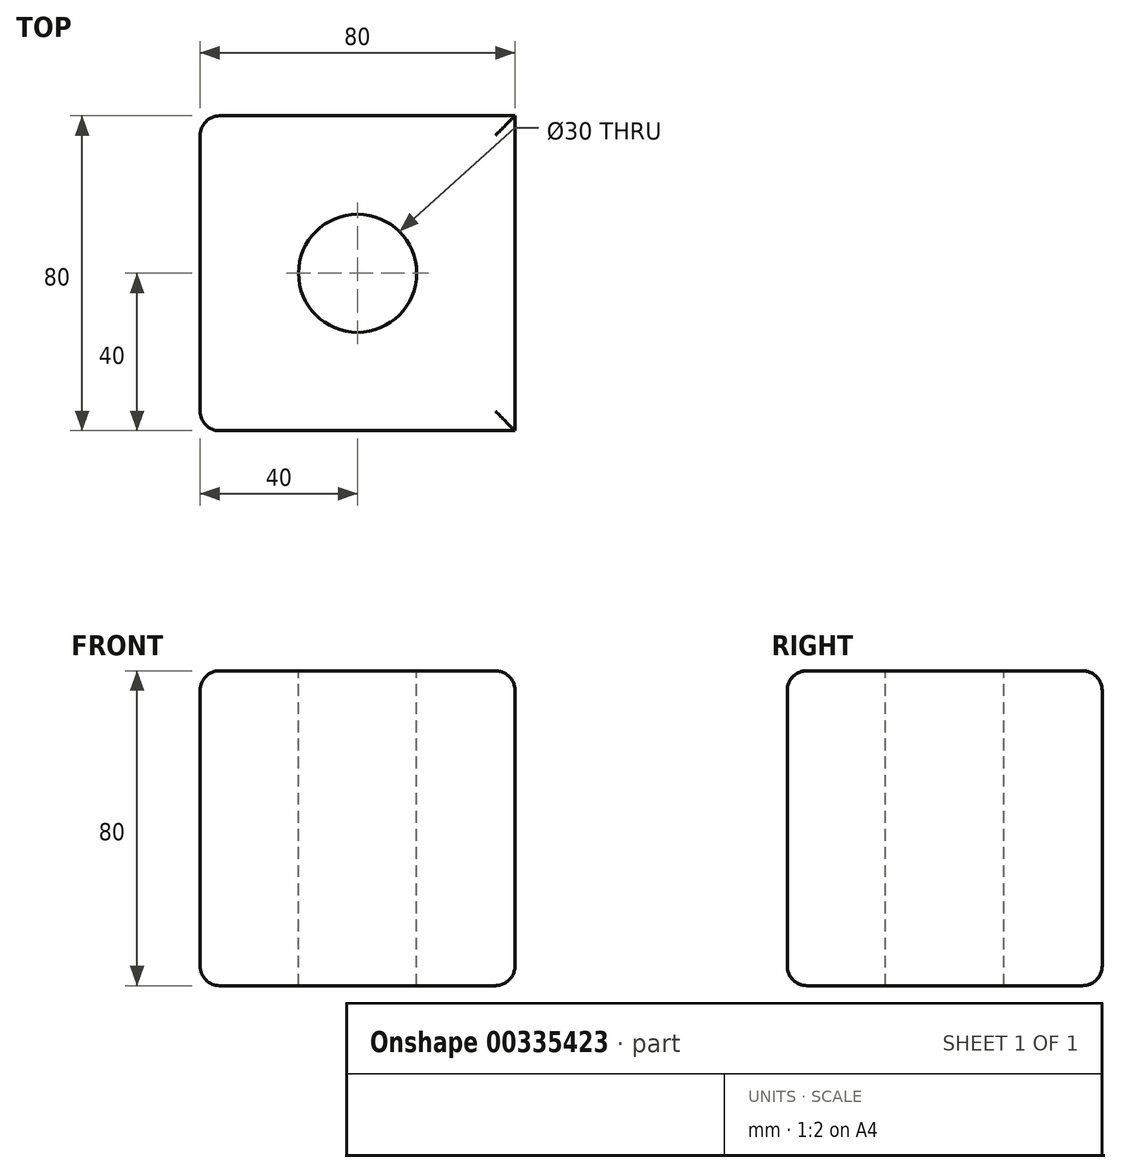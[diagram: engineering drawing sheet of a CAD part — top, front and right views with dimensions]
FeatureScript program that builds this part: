
annotation { "Feature Type Name" : "Feature", "Feature Type Description" : "" }
export const myFeature = defineFeature(function(context is Context, id is Id, definition is map)
    precondition{}
    {
        {
            var Q0;
            Q0=qCreatedBy(makeId("Top.planeOp"),FACE);
            var sketch = newSketch(context, id + "F0", { "sketchPlane" : qUnion([Q0])});
            skLineSegment(sketch, "E0.bottom", {"start": v(-40, -40) * mm, "end": v(40, -40) * mm});
            skLineSegment(sketch, "E0.top", {"start": v(-40, 40) * mm, "end": v(40, 40) * mm});
            skLineSegment(sketch, "E0.left", {"start": v(-40, -40) * mm, "end": v(-40, 40) * mm});
            skLineSegment(sketch, "E0.right", {"start": v(40, -40) * mm, "end": v(40, 40) * mm});
            skPoint(sketch, "E0.middle", {"position": v(0, 0) * mm});
            skSolve(sketch);
        }
        {
            var Q0;
            Q0=makeQuery(id+"F0.imprint","IMPRINT",FACE,{"disambiguationData":[TD([[makeQuery(id+"F0.imprint","IMPRINT",EDGE,{"derivedFrom":sQuery(id+"F0.wireOp",EDGE,"E0.bottom")}),1.0]])]});
            extrude(context, id + "F1", {"entities" : qUnion([Q0]), "endBound" : BoundingType.SYMMETRIC, "depth" : 80 * mm});
        }
        {
            var Q0;
            Q0=makeQuery(id+"F1.opExtrude","CAP_EDGE",EDGE,{"disambiguationData":[OSD([sQuery(id+"F0.wireOp",EDGE,"E0.right")])],"isStart":false});
            var Q1;
            Q1=makeQuery(id+"F1.opExtrude","CAP_EDGE",EDGE,{"disambiguationData":[OSD([sQuery(id+"F0.wireOp",EDGE,"E0.top")])],"isStart":false});
            var Q2;
            Q2=makeQuery(id+"F1.opExtrude","CAP_EDGE",EDGE,{"disambiguationData":[OSD([sQuery(id+"F0.wireOp",EDGE,"E0.left")])],"isStart":false});
            var Q3;
            Q3=makeQuery(id+"F1.opExtrude","CAP_EDGE",EDGE,{"disambiguationData":[OSD([sQuery(id+"F0.wireOp",EDGE,"E0.bottom")])],"isStart":false});
            var Q4;
            Q4=makeQuery(id+"F1.opExtrude","CAP_FACE",FACE,{"disambiguationData":[OSD([sQuery(id+"F0.wireOp",EDGE,"E0.bottom"),sQuery(id+"F0.wireOp",EDGE,"E0.top"),sQuery(id+"F0.wireOp",EDGE,"E0.left"),sQuery(id+"F0.wireOp",EDGE,"E0.right")])],"isStart":false});
            var Q5;
            Q5=makeQuery(id+"F1.opExtrude","SWEPT_EDGE",EDGE,{"disambiguationData":[OSD([sQuery(id+"F0.wireOp",EDGE,"E0.top"),sQuery(id+"F0.wireOp",EDGE,"E0.left")])]});
            var Q6;
            Q6=makeQuery(id+"F1.opExtrude","CAP_EDGE",EDGE,{"disambiguationData":[OSD([sQuery(id+"F0.wireOp",EDGE,"E0.left")])],"isStart":true});
            var Q7;
            Q7=makeQuery(id+"F1.opExtrude","SWEPT_EDGE",EDGE,{"disambiguationData":[OSD([sQuery(id+"F0.wireOp",EDGE,"E0.bottom"),sQuery(id+"F0.wireOp",EDGE,"E0.left")])]});
            var Q8;
            Q8=makeQuery(id+"F1.opExtrude","CAP_EDGE",EDGE,{"disambiguationData":[OSD([sQuery(id+"F0.wireOp",EDGE,"E0.top")])],"isStart":true});
            var Q9;
            Q9=makeQuery(id+"F1.opExtrude","CAP_EDGE",EDGE,{"disambiguationData":[OSD([sQuery(id+"F0.wireOp",EDGE,"E0.bottom")])],"isStart":true});
            var Q10;
            Q10=makeQuery(id+"F1.opExtrude","CAP_EDGE",EDGE,{"disambiguationData":[OSD([sQuery(id+"F0.wireOp",EDGE,"E0.right")])],"isStart":true});
            var Q11;
            Q11=makeQuery(id+"F1.opExtrude","CAP_FACE",FACE,{"disambiguationData":[OSD([sQuery(id+"F0.wireOp",EDGE,"E0.bottom"),sQuery(id+"F0.wireOp",EDGE,"E0.top"),sQuery(id+"F0.wireOp",EDGE,"E0.left"),sQuery(id+"F0.wireOp",EDGE,"E0.right")])],"isStart":true});
            fillet(context, id + "F2", {"entities" : qUnion([Q0, Q1, Q2, Q3, Q4, Q5, Q6, Q7, Q8, Q9, Q10, Q11]), "radius" : 5 * mm, "tangentPropagation" : true, "allowEdgeOverflow" : false});
        }
        {
            var Q0;
            Q0=makeQuery(id+"F1.opExtrude","CAP_FACE",FACE,{"disambiguationData":[OSD([sQuery(id+"F0.wireOp",EDGE,"E0.bottom"),sQuery(id+"F0.wireOp",EDGE,"E0.top"),sQuery(id+"F0.wireOp",EDGE,"E0.left"),sQuery(id+"F0.wireOp",EDGE,"E0.right")])],"isStart":false});
            var sketch = newSketch(context, id + "F3", { "sketchPlane" : qUnion([Q0])});
            skCircle(sketch, "E1", {"center": v(0, 0) * mm, "radius": 15 * mm});
            skSolve(sketch);
        }
        {
            var Q0;
            Q0=makeQuery(id+"F3.imprint","IMPRINT",FACE,{"disambiguationData":[TD([[makeQuery(id+"F3.imprint","IMPRINT",EDGE,{"derivedFrom":sQuery(id+"F3.wireOp",EDGE,"E1")}),1.0]])]});
            extrude(context, id + "F4", {"entities" : qUnion([Q0]), "operationType" : NewBodyOperationType.REMOVE, "endBound" : BoundingType.THROUGH_ALL, "oppositeDirection" : true, "depth" : 25 * mm});
        }
    });
